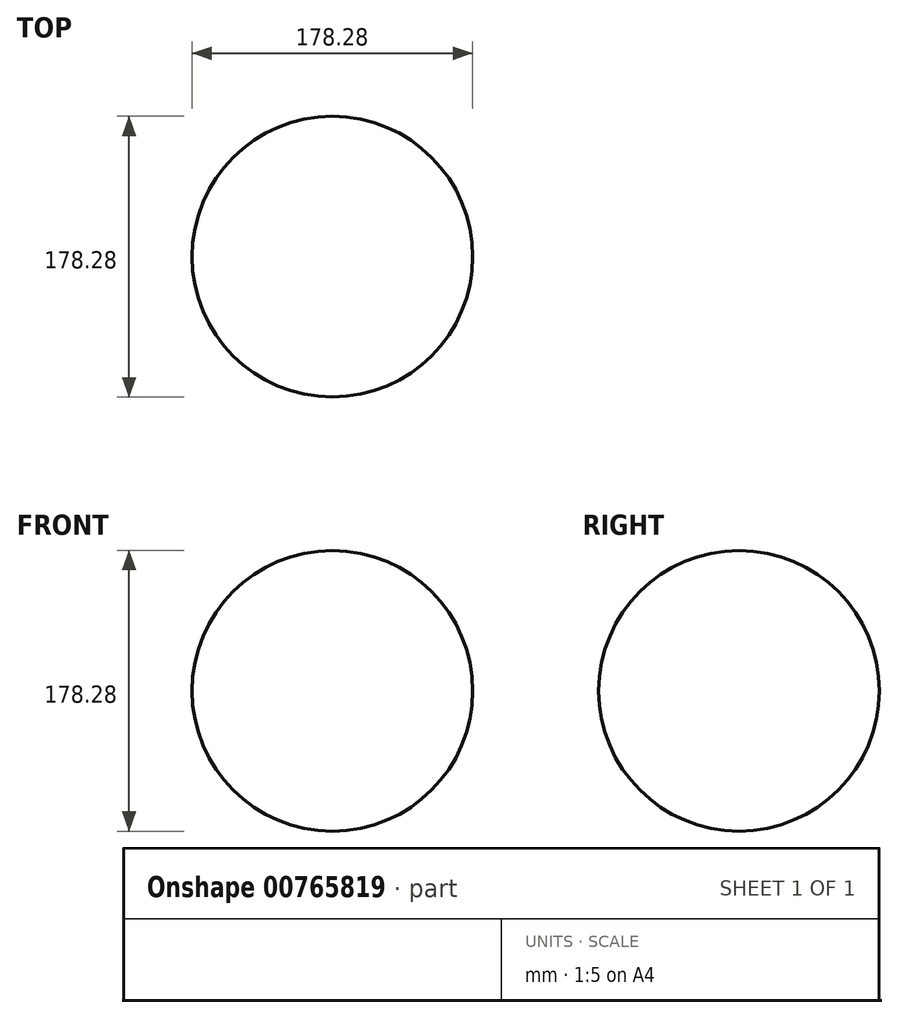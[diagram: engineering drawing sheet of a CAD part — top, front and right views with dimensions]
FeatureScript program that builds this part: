
annotation { "Feature Type Name" : "Feature", "Feature Type Description" : "" }
export const myFeature = defineFeature(function(context is Context, id is Id, definition is map)
    precondition{}
    {
        {
            var Q0;
            Q0=qCreatedBy(makeId("Front.planeOp"),FACE);
            var sketch = newSketch(context, id + "F0", { "sketchPlane" : qUnion([Q0])});
            skCircle(sketch, "E0", {"center": v(0, 0) * mm, "radius": 89.14 * mm});
            skLineSegment(sketch, "E1", {"start": v(0, 89.14) * mm, "end": v(0, -89.14) * mm});
            skSolve(sketch);
        }
        {
            var Q0;
            {var subQ0=sQuery(id+"F0.wireOp",EDGE,"E1");Q0=makeQuery(id+"F0.imprint","IMPRINT",FACE,{"disambiguationData":[TD([[makeQuery(id+"F0.imprint","IMPRINT",EDGE,{"derivedFrom":subQ0}),-1.0]])]});}
            var Q1;
            Q1=sQuery(id+"F0.wireOp",EDGE,"E1");
            revolve(context, id + "F1", {"surfaceOperationType" : NewSurfaceOperationType.NEW, "entities" : qUnion([Q0]), "axis" : qUnion([Q1]), "revolveType" : RevolveType.FULL});
        }
    });
